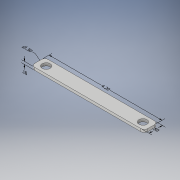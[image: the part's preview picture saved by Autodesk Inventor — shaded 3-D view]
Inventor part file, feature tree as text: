
AUTODESK INVENTOR PART (.ipt)
format: ipt  version: 2018 (Build 220112000, 112)  size: 134,144 bytes
history: native  units: in
note: dims shown in document units (in); Inventor stores cm internally (conversion verified against a paired STEP export)
features: other x5, sketch x3, extrude x2, fillet x1, hole x1
ambient origin geometry x8: Origin, YZ Plane, XZ Plane, XY Plane, X Axis, Y Axis, Z Axis, Center Point
bodies: Solid1 (feature_tree)
feature tree (12):
  other  "Annotations"
  extrude  "Extrusion1"  Depth=0.5in
  fillet  "Fillet1"  Radius=0.1in
  extrude  "Extrusion2"  Depth=0.125in
  hole  "Hole1"  [1 undecoded]
  sketch  "Sketch1"  dims[d0=4.2in d1=0.5in d2=0.1in d3=0.0in]
  sketch  "Sketch2"  dims[d4=0.125in d5=0.3in]
  sketch  "Sketch3"  dims[d6=0.3in d7=0.3in d8=0.3in d9=0.1in d10=0.0in d11=0.3in d12=0.3in d13=0.3in d14=0.75in d15=0.375in d16=0.25in d17=0.5635in d18=1.0in d19=0.8108in d20=0.0931in d21=0.0926in d22=0.1in d23=1.284in d24=0.3in d25=0.185in d26=0.2423in d27=4.2in d28=0.0503in d29=0.3397in d30=0.5in]
  other  "Linear Dimension 1"
  other  "Diameter Dimension 1"
  other  "Linear Dimension 2"
  other  "Linear Dimension 3"
note: 1 required parameter value undecoded (feature->parameter linkage not recoverable at this tier; creation-order binding heuristic only, values carry confidence <= 0.55)
